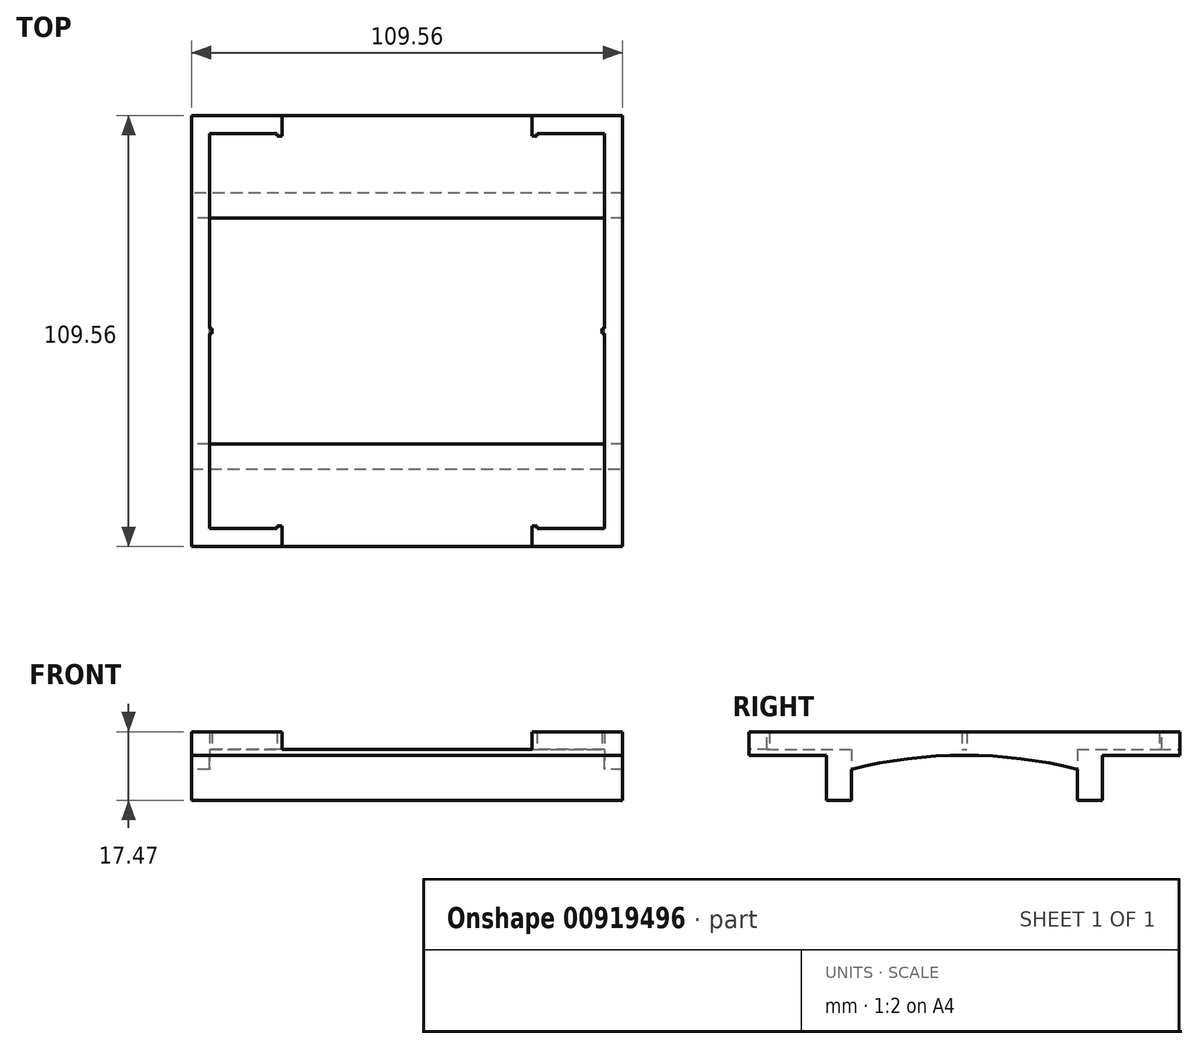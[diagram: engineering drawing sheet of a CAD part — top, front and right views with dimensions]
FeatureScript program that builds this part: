
annotation { "Feature Type Name" : "Feature", "Feature Type Description" : "" }
export const myFeature = defineFeature(function(context is Context, id is Id, definition is map)
    precondition{}
    {
        {
            var Q0;
            Q0=qCreatedBy(makeId("Right.planeOp"),FACE);
            var sketch = newSketch(context, id + "F0", { "sketchPlane" : qUnion([Q0])});
            skLineSegment(sketch, "E0", {"start": v(-35.05, 9.53) * mm, "end": v(-35.05, -7.94) * mm});
            skLineSegment(sketch, "E1", {"start": v(-35.05, -7.94) * mm, "end": v(-28.7, -7.94) * mm});
            skLineSegment(sketch, "E2", {"start": v(-28.7, -7.94) * mm, "end": v(-28.7, 0) * mm});
            skLineSegment(sketch, "E3", {"start": v(-28.7, 0) * mm, "end": v(28.7, 0) * mm});
            skLineSegment(sketch, "E4", {"start": v(28.7, 0) * mm, "end": v(28.7, -7.94) * mm});
            skLineSegment(sketch, "E5", {"start": v(28.7, -7.94) * mm, "end": v(35.05, -7.94) * mm});
            skLineSegment(sketch, "E6", {"start": v(35.05, -7.94) * mm, "end": v(35.05, 9.53) * mm});
            skLineSegment(sketch, "E7", {"start": v(-35.05, 9.53) * mm, "end": v(35.05, 9.53) * mm});
            skSolve(sketch);
        }
        {
            var Q0;
            Q0=makeQuery(id+"F0.imprint","IMPRINT",FACE,{"disambiguationData":[TD([[makeQuery(id+"F0.imprint","IMPRINT",EDGE,{"derivedFrom":sQuery(id+"F0.wireOp",EDGE,"E0")}),1.0]])]});
            extrude(context, id + "F1", {"entities" : qUnion([Q0]), "depth" : 54.78 * mm, "offsetDistance" : 25.4 * mm, "hasSecondDirection" : true, "secondDirectionOppositeDirection" : true, "secondDirectionDepth" : 54.78 * mm});
        }
        {
            var Q0;
            Q0=qCreatedBy(makeId("Right.planeOp"),FACE);
            var sketch = newSketch(context, id + "F2", { "sketchPlane" : qUnion([Q0])});
            skArc(sketch, "E8", {"start": v(-28.7, 0) * mm, "mid": v(0, 3.55) * mm, "end": v(28.7, 0) * mm});
            skLineSegment(sketch, "E9", {"start": v(-28.7, 0) * mm, "end": v(28.7, 0) * mm});
            skSolve(sketch);
        }
        {
            var Q0;
            Q0 = qSketchRegion(id + "F2", true);
            extrude(context, id + "F3", {"entities" : qUnion([Q0]), "operationType" : NewBodyOperationType.REMOVE, "endBound" : BoundingType.THROUGH_ALL, "depth" : 25.4 * mm, "offsetDistance" : 25.4 * mm, "hasSecondDirection" : true, "secondDirectionBound" : SecondDirectionBoundingType.THROUGH_ALL, "secondDirectionOppositeDirection" : true, "secondDirectionDepth" : 25.4 * mm});
        }
        {
            var Q0;
            Q0=qCreatedBy(makeId("Right.planeOp"),FACE);
            var sketch = newSketch(context, id + "F4", { "sketchPlane" : qUnion([Q0])});
            skLineSegment(sketch, "E10.bottom", {"start": v(54.78, 9.53) * mm, "end": v(-54.78, 9.52) * mm});
            skPoint(sketch, "E10.middle", {"position": v(0, 3.97) * mm});
            skLineSegment(sketch, "E11", {"start": v(-54.78, 9.52) * mm, "end": v(-54.78, 3.55) * mm});
            skLineSegment(sketch, "E12", {"start": v(-54.78, 3.55) * mm, "end": v(54.78, 3.55) * mm});
            skLineSegment(sketch, "E13", {"start": v(54.78, 3.55) * mm, "end": v(54.78, 9.53) * mm});
            skLineSegment(sketch, "E14", {"start": v(0, 9.52) * mm, "end": v(0, 3.55) * mm, "construction": true});
            skSolve(sketch);
        }
        {
            var Q0;
            Q0=makeQuery(id+"F4.imprint","IMPRINT",FACE,{"disambiguationData":[TD([[makeQuery(id+"F4.imprint","IMPRINT",EDGE,{"derivedFrom":sQuery(id+"F4.wireOp",EDGE,"E10.bottom")}),1.0]])]});
            var Q1;
            Q1=makeQuery(id+"F1.opExtrude","CAP_FACE",FACE,{"disambiguationData":[OSD([sQuery(id+"F0.wireOp",EDGE,"E0"),sQuery(id+"F0.wireOp",EDGE,"E1"),sQuery(id+"F0.wireOp",EDGE,"E2"),sQuery(id+"F0.wireOp",EDGE,"E3"),sQuery(id+"F0.wireOp",EDGE,"E4"),sQuery(id+"F0.wireOp",EDGE,"E5"),sQuery(id+"F0.wireOp",EDGE,"E6"),sQuery(id+"F0.wireOp",EDGE,"Ht9ldmMr-KXzw-w7Vc-ak45-NHIThXfTsuMc")])],"isStart":false});
            var Q2;
            Q2=makeQuery(id+"F1.opExtrude","CAP_FACE",FACE,{"disambiguationData":[OSD([sQuery(id+"F0.wireOp",EDGE,"E0"),sQuery(id+"F0.wireOp",EDGE,"E1"),sQuery(id+"F0.wireOp",EDGE,"E2"),sQuery(id+"F0.wireOp",EDGE,"E3"),sQuery(id+"F0.wireOp",EDGE,"E4"),sQuery(id+"F0.wireOp",EDGE,"E5"),sQuery(id+"F0.wireOp",EDGE,"E6"),sQuery(id+"F0.wireOp",EDGE,"Ht9ldmMr-KXzw-w7Vc-ak45-NHIThXfTsuMc")])],"isStart":true});
            extrude(context, id + "F5", {"entities" : qUnion([Q0]), "operationType" : NewBodyOperationType.ADD, "endBound" : BoundingType.UP_TO_SURFACE, "depth" : 25.4 * mm, "endBoundEntityFace" : qUnion([Q1]), "offsetDistance" : 25.4 * mm, "hasSecondDirection" : true, "secondDirectionBound" : SecondDirectionBoundingType.UP_TO_SURFACE, "secondDirectionOppositeDirection" : true, "secondDirectionDepth" : 25.4 * mm, "secondDirectionBoundEntityFace" : qUnion([Q2])});
        }
        {
            var Q0;
            Q0=makeQuery(id+"F5.opExtrude","SWEPT_FACE",FACE,{"disambiguationData":[OSD([sQuery(id+"F4.wireOp",EDGE,"E10.bottom")])]});
            var sketch = newSketch(context, id + "F6", { "sketchPlane" : qUnion([Q0])});
            skLineSegment(sketch, "E15.left", {"start": v(50.16, 50.17) * mm, "end": v(50.17, -50.16) * mm});
            skLineSegment(sketch, "E15.right", {"start": v(-50.17, 50.16) * mm, "end": v(-50.16, -50.17) * mm});
            skPoint(sketch, "E15.middle", {"position": v(0, 0) * mm});
            skLineSegment(sketch, "E16", {"start": v(-50.17, 50.16) * mm, "end": v(-31.75, 50.16) * mm});
            skLineSegment(sketch, "E17", {"start": v(-31.75, 50.17) * mm, "end": v(-31.75, 54.78) * mm});
            skLineSegment(sketch, "E18", {"start": v(-31.75, 54.78) * mm, "end": v(31.75, 54.78) * mm});
            skLineSegment(sketch, "E19", {"start": v(31.75, 54.78) * mm, "end": v(31.75, 50.17) * mm});
            skLineSegment(sketch, "E20", {"start": v(31.75, 50.17) * mm, "end": v(50.16, 50.17) * mm});
            skLineSegment(sketch, "E21", {"start": v(0, -54.78) * mm, "end": v(0, 54.78) * mm, "construction": true});
            skLineSegment(sketch, "E22", {"start": v(-50.16, -50.17) * mm, "end": v(-31.75, -50.17) * mm});
            skLineSegment(sketch, "E23", {"start": v(-31.75, -50.17) * mm, "end": v(-31.75, -54.78) * mm});
            skLineSegment(sketch, "E24", {"start": v(-31.75, -54.78) * mm, "end": v(31.75, -54.78) * mm});
            skLineSegment(sketch, "E25", {"start": v(31.75, -54.78) * mm, "end": v(31.75, -50.17) * mm});
            skLineSegment(sketch, "E26", {"start": v(31.75, -50.16) * mm, "end": v(50.17, -50.16) * mm});
            skLineSegment(sketch, "E27", {"start": v(50.17, 0) * mm, "end": v(0, 0) * mm, "construction": true});
            skSolve(sketch);
        }
        {
            var Q0;
            Q0 = qSketchRegion(id + "F6", true);
            var Q1;
            {var subQ1=sQuery(id+"F4.wireOp",EDGE,"E12");var subQ11=sQuery(id+"F0.wireOp",EDGE,"E0");Q1=makeQuery(id+"F5.boolean.opBoolean","SPLIT",FACE,{"disambiguationData":[TD([makeQuery(id+"F1.opExtrude","SWEPT_FACE",FACE,{"disambiguationData":[OSD([subQ11])]})])],"derivedFrom":makeQuery(id+"F5.opExtrude","SWEPT_FACE",FACE,{"disambiguationData":[OSD([subQ1])]})});}
            extrude(context, id + "F7", {"entities" : qUnion([Q0]), "operationType" : NewBodyOperationType.REMOVE, "endBound" : BoundingType.UP_TO_SURFACE, "oppositeDirection" : true, "depth" : 5.08 * mm, "endBoundEntityFace" : qUnion([Q1]), "hasOffset" : true, "offsetDistance" : 1.52 * mm});
        }
        {
            var Q0;
            Q0=qCreatedBy(makeId("Right.planeOp"),FACE);
            var sketch = newSketch(context, id + "F8", { "sketchPlane" : qUnion([Q0])});
            skLineSegment(sketch, "E28.bottom", {"start": v(-28.7, -7.94) * mm, "end": v(28.7, -7.94) * mm});
            skLineSegment(sketch, "E28.top", {"start": v(-28.7, 9.53) * mm, "end": v(28.7, 9.53) * mm});
            skLineSegment(sketch, "E28.left", {"start": v(-28.7, -7.94) * mm, "end": v(-28.7, 9.53) * mm});
            skLineSegment(sketch, "E28.right", {"start": v(28.7, -7.94) * mm, "end": v(28.7, 9.53) * mm});
            skSolve(sketch);
        }
        {
            var Q0;
            Q0 = qSketchRegion(id + "F8", true);
            var Q1;
            Q1=makeQuery(id+"F7.boolean.opBoolean","COPY",FACE,{"derivedFrom":makeQuery(id+"F7.opExtrude","SWEPT_FACE",FACE,{"disambiguationData":[OSD([sQuery(id+"F6.wireOp",EDGE,"E15.left")])]})});
            var Q2;
            Q2=makeQuery(id+"F7.boolean.opBoolean","COPY",FACE,{"derivedFrom":makeQuery(id+"F7.opExtrude","SWEPT_FACE",FACE,{"disambiguationData":[OSD([sQuery(id+"F6.wireOp",EDGE,"E15.right")])]})});
            extrude(context, id + "F9", {"entities" : qUnion([Q0]), "operationType" : NewBodyOperationType.REMOVE, "endBound" : BoundingType.UP_TO_SURFACE, "depth" : 50.8 * mm, "endBoundEntityFace" : qUnion([Q1]), "offsetDistance" : 25.4 * mm, "hasSecondDirection" : true, "secondDirectionBound" : SecondDirectionBoundingType.UP_TO_SURFACE, "secondDirectionOppositeDirection" : true, "secondDirectionDepth" : 25.4 * mm, "secondDirectionBoundEntityFace" : qUnion([Q2])});
        }
        {
            var Q0;
            {var subQ0=sQuery(id+"F6.wireOp",EDGE,"E20");var subQ5=sQuery(id+"F6.wireOp",EDGE,"E19");var subQ6=sQuery(id+"F6.wireOp",EDGE,"E17");var subQ7=sQuery(id+"F6.wireOp",EDGE,"E16");var subQ8=sQuery(id+"F6.wireOp",EDGE,"E15.left");var subQ9=sQuery(id+"F6.wireOp",EDGE,"E15.right");Q0=makeQuery(id+"F9.boolean.opBoolean","SPLIT",FACE,{"disambiguationData":[TD([makeQuery(id+"F1.opExtrude","SWEPT_FACE",FACE,{"disambiguationData":[OSD([sQuery(id+"F0.wireOp",EDGE,"E4")])]})])],"derivedFrom":makeQuery(id+"F7.boolean.opBoolean","COPY",FACE,{"derivedFrom":makeQuery(id+"F7.opExtrude","CAP_FACE",FACE,{"disambiguationData":[OSD([subQ8,subQ9,subQ7,subQ6,sQuery(id+"F6.wireOp",EDGE,"E18"),subQ5,subQ0,sQuery(id+"F6.wireOp",EDGE,"E22"),sQuery(id+"F6.wireOp",EDGE,"E23"),sQuery(id+"F6.wireOp",EDGE,"E24"),sQuery(id+"F6.wireOp",EDGE,"E25"),sQuery(id+"F6.wireOp",EDGE,"E26")])],"isStart":false})})});}
            var sketch = newSketch(context, id + "F10", { "sketchPlane" : qUnion([Q0])});
            skLineSegment(sketch, "E29.bottom", {"start": v(-31.75, 50.16) * mm, "end": v(-33.02, 50.16) * mm});
            skLineSegment(sketch, "E29.top", {"start": v(-31.75, 49.53) * mm, "end": v(-33.02, 49.53) * mm});
            skLineSegment(sketch, "E29.left", {"start": v(-31.75, 50.16) * mm, "end": v(-31.75, 49.53) * mm});
            skLineSegment(sketch, "E29.right", {"start": v(-33.02, 50.16) * mm, "end": v(-33.02, 49.53) * mm});
            skLineSegment(sketch, "E30.bottom", {"start": v(31.75, 50.17) * mm, "end": v(33.02, 50.17) * mm});
            skLineSegment(sketch, "E30.top", {"start": v(31.75, 49.53) * mm, "end": v(33.02, 49.53) * mm});
            skLineSegment(sketch, "E30.left", {"start": v(31.75, 50.17) * mm, "end": v(31.75, 49.53) * mm});
            skLineSegment(sketch, "E30.right", {"start": v(33.02, 50.17) * mm, "end": v(33.02, 49.53) * mm});
            skLineSegment(sketch, "E31.bottom", {"start": v(-31.75, -50.17) * mm, "end": v(-33.02, -50.17) * mm});
            skLineSegment(sketch, "E31.top", {"start": v(-31.75, -49.53) * mm, "end": v(-33.02, -49.53) * mm});
            skLineSegment(sketch, "E31.left", {"start": v(-31.75, -50.17) * mm, "end": v(-31.75, -49.53) * mm});
            skLineSegment(sketch, "E31.right", {"start": v(-33.02, -50.17) * mm, "end": v(-33.02, -49.53) * mm});
            skLineSegment(sketch, "E32.bottom", {"start": v(31.75, -50.16) * mm, "end": v(33.02, -50.16) * mm});
            skLineSegment(sketch, "E32.top", {"start": v(31.75, -49.53) * mm, "end": v(33.02, -49.53) * mm});
            skLineSegment(sketch, "E32.left", {"start": v(31.75, -50.16) * mm, "end": v(31.75, -49.53) * mm});
            skLineSegment(sketch, "E32.right", {"start": v(33.02, -50.16) * mm, "end": v(33.02, -49.53) * mm});
            skLineSegment(sketch, "E33.bottom", {"start": v(-50.17, -0.63) * mm, "end": v(-49.53, -0.63) * mm});
            skLineSegment(sketch, "E33.top", {"start": v(-50.17, 0.64) * mm, "end": v(-49.53, 0.64) * mm});
            skLineSegment(sketch, "E33.left", {"start": v(-50.17, -0.63) * mm, "end": v(-50.17, 0.64) * mm});
            skLineSegment(sketch, "E33.right", {"start": v(-49.53, -0.63) * mm, "end": v(-49.53, 0.64) * mm});
            skLineSegment(sketch, "E34.bottom", {"start": v(50.17, -0.63) * mm, "end": v(49.53, -0.63) * mm});
            skLineSegment(sketch, "E34.top", {"start": v(50.17, 0.64) * mm, "end": v(49.53, 0.64) * mm});
            skLineSegment(sketch, "E34.left", {"start": v(50.17, -0.63) * mm, "end": v(50.17, 0.64) * mm});
            skLineSegment(sketch, "E34.right", {"start": v(49.53, -0.63) * mm, "end": v(49.53, 0.64) * mm});
            skLineSegment(sketch, "E35", {"start": v(-49.53, 0) * mm, "end": v(49.53, 0) * mm, "construction": true});
            skSolve(sketch);
        }
        {
            var Q0;
            Q0 = qSketchRegion(id + "F10", true);
            var Q1;
            {var subQ2=sQuery(id+"F4.wireOp",EDGE,"E10.bottom");var subQ3=sQuery(id+"F0.wireOp",EDGE,"E7");Q1=makeQuery(id+"F7.boolean.opBoolean","SPLIT",FACE,{"disambiguationData":[TD([makeQuery(id+"F7.opExtrude","SWEPT_FACE",FACE,{"disambiguationData":[OSD([sQuery(id+"F6.wireOp",EDGE,"E15.right")])]})])],"derivedFrom":makeQuery(id+"F5.boolean.opBoolean","MERGE",FACE,{"derivedFrom":[makeQuery(id+"F1.opExtrude","SWEPT_FACE",FACE,{"disambiguationData":[OSD([subQ3])]}),makeQuery(id+"F5.opExtrude","SWEPT_FACE",FACE,{"disambiguationData":[OSD([subQ2])]})]})});}
            extrude(context, id + "F11", {"entities" : qUnion([Q0]), "operationType" : NewBodyOperationType.ADD, "endBound" : BoundingType.UP_TO_SURFACE, "depth" : 25.4 * mm, "endBoundEntityFace" : qUnion([Q1]), "offsetDistance" : 25.4 * mm});
        }
    });
